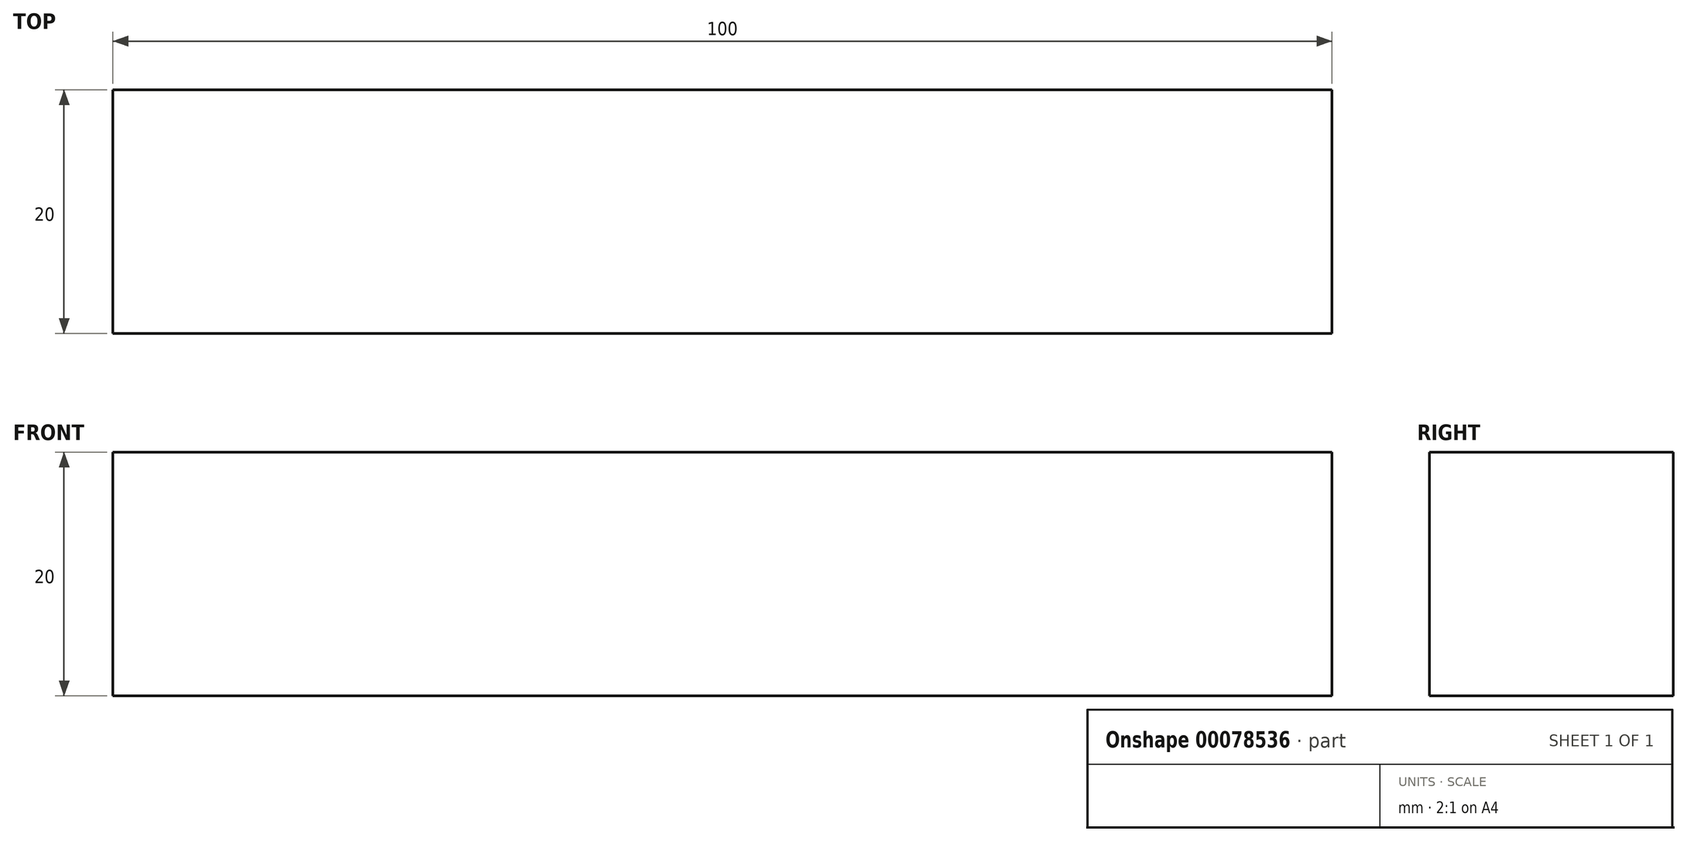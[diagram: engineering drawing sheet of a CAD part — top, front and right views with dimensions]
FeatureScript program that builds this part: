
annotation { "Feature Type Name" : "Feature", "Feature Type Description" : "" }
export const myFeature = defineFeature(function(context is Context, id is Id, definition is map)
    precondition{}
    {
        {
            var Q0;
            Q0=qCreatedBy(makeId("Top.planeOp"),FACE);
            var sketch = newSketch(context, id + "F0", { "sketchPlane" : qUnion([Q0])});
            skLineSegment(sketch, "E0.bottom", {"start": v(-50, 10) * mm, "end": v(50, 10) * mm});
            skLineSegment(sketch, "E0.top", {"start": v(-50, -10) * mm, "end": v(50, -10) * mm});
            skLineSegment(sketch, "E0.left", {"start": v(-50, 10) * mm, "end": v(-50, -10) * mm});
            skLineSegment(sketch, "E0.right", {"start": v(50, 10) * mm, "end": v(50, -10) * mm});
            skPoint(sketch, "E0.middle", {"position": v(0, 0) * mm});
            skSolve(sketch);
        }
        {
            var Q0;
            Q0=makeQuery(id+"F0.imprint","IMPRINT",FACE,{"disambiguationData":[TD([[makeQuery(id+"F0.imprint","IMPRINT",EDGE,{"derivedFrom":sQuery(id+"F0.wireOp",EDGE,"E0.bottom")}),-1.0]])]});
            extrude(context, id + "F1", {"entities" : qUnion([Q0]), "depth" : 20 * mm});
        }
    });
